# Revit family: QDAR
name_source: partatom
category: Lighting Fixtures
units: mm (PartAtom-declared; Revit-internal decimal feet)

## family parameters
Always vertical = Yes
Cut with Voids When Loaded = No
Host = Ceiling
Light Source = Yes
OmniClass Number = 23.80.70.11.14.17
OmniClass Title = Direct/Indirect
Part Type = Normal
Room Calculation Point = No
Round Connector Dimension = Use Diameter
Shared = No

## types (15) — shared parameters
Assembly Code = D5020200
Color Filter = 16777215
Description = Quadra Recessed Drop Lens
Dimming Lamp Color Temperature Shift = <None>
Emit Shape Visible in Rendering = No
Emit from Rectangle Length = 1' - 11 3/4"
Emit from Rectangle Width = 1' - 11 3/4"
Housing Finish = Metal - Viscor - White
Lamp = LED
Length = 1' - 11 3/4"
Lens Finish = Acrylic - Viscor - Opal White Square
Manufacturer = VISIONEERING by VISCOR
Model = QDAR
Tilt Angle = 90.00°
URL = https://www.viscor.com
Voltage = 120 V
Width = 1' - 11 3/4"

## per-type parameters (varying)
| type | Apparent Load | Emit from Rectangle Height | Lamp Wattage | Lens Depth | Photometric Web File |
| QDAR2X2D0-LED840K020LUNV | 19 VA | 0' - 0 1/32" | 19 VA | 0' - 0 1/32" | QDAR2X2D0-LED840K20LUNV.ies |
| QDAR2X2D0-LED840K030LUNV | 27 VA | 0' - 0 1/32" | 27 VA | 0' - 0 1/32" | QDAR2X2D0-LED840K30LUNV.ies |
| QDAR2X2D0-LED840K040LUNV | 36 VA | 0' - 0 1/32" | 36 VA | 0' - 0 1/32" | QDAR2X2D0-LED840K40LUNV.ies |
| QDAR2X2D1-LED840K020LUNV | 19 VA | 0' - 1" | 19 VA | 0' - 1" | QDAR2X2D1-LED840K20LUNV.ies |
| QDAR2X2D1-LED840K030LUNV | 27 VA | 0' - 1" | 27 VA | 0' - 1" | QDAR2X2D1-LED840K30LUNV.ies |
| QDAR2X2D1-LED840K040LUNV | 36 VA | 0' - 1" | 36 VA | 0' - 1" | QDAR2X2D1-LED840K40LUNV.ies |
| QDAR2X2D2-LED840K020LUNV | 19 VA | 0' - 2" | 19 VA | 0' - 2" | QDAR2X2D2-LED840K20LUNV.ies |
| QDAR2X2D2-LED840K030LUNV | 27 VA | 0' - 2" | 27 VA | 0' - 2" | QDAR2X2D2-LED840K30LUNV.ies |
| QDAR2X2D2-LED840K040LUNV | 36 VA | 0' - 2" | 36 VA | 0' - 2" | QDAR2X2D2-LED840K40LUNV.ies |
| QDAR2X2D3-LED840K020LUNV | 19 VA | 0' - 3" | 19 VA | 0' - 3" | QDAR2X2D3-LED840K20LUNV.ies |
| QDAR2X2D3-LED840K030LUNV | 27 VA | 0' - 3" | 27 VA | 0' - 3" | QDAR2X2D3-LED840K30LUNV.ies |
| QDAR2X2D3-LED840K040LUNV | 36 VA | 0' - 3" | 36 VA | 0' - 3" | QDAR2X2D3-LED840K40LUNV.ies |
| QDAR2X2D4-LED840K020LUNV | 19 VA | 0' - 4" | 19 VA | 0' - 4" | QDAR2X2D4-LED840K20LUNV.ies |
| QDAR2X2D4-LED840K030LUNV | 27 VA | 0' - 4" | 27 VA | 0' - 4" | QDAR2X2D4-LED840K30LUNV.ies |
| QDAR2X2D4-LED840K040LUNV | 36 VA | 0' - 4" | 36 VA | 0' - 4" | QDAR2X2D4-LED840K40LUNV.ies |

## geometry (parser evidence)
native form markers: Sweep x3
no freeform markers — native parametric forms only
